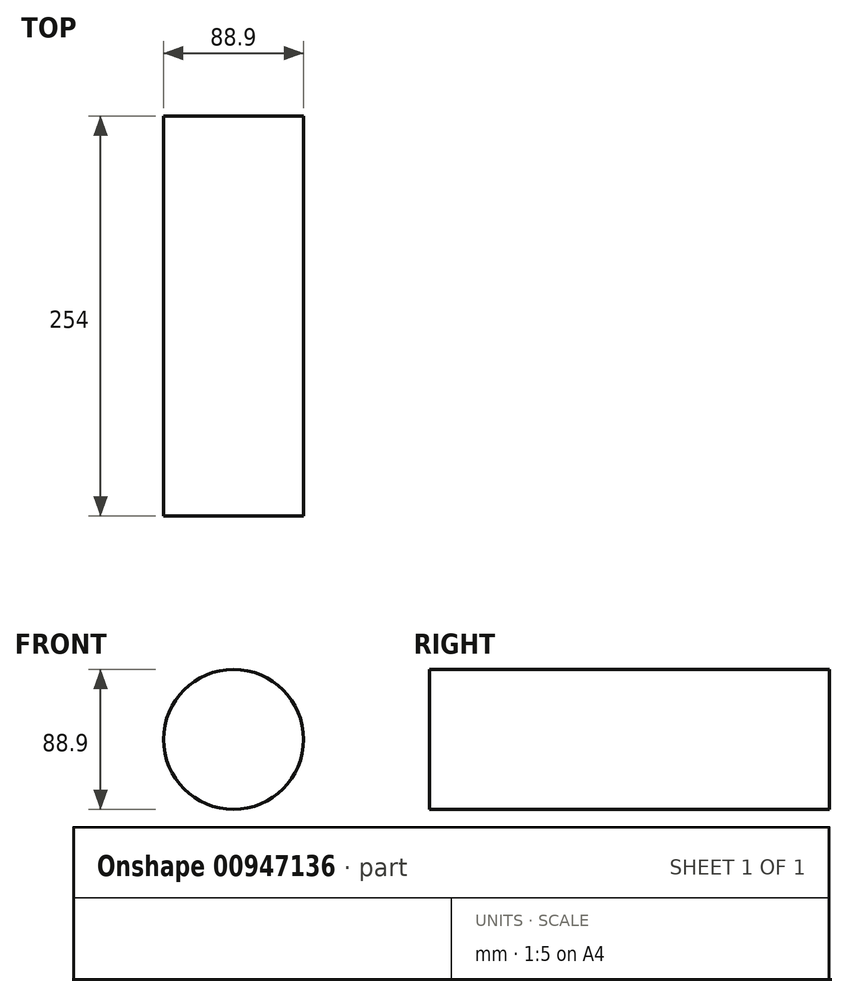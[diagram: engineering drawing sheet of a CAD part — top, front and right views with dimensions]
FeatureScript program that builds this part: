
annotation { "Feature Type Name" : "Feature", "Feature Type Description" : "" }
export const myFeature = defineFeature(function(context is Context, id is Id, definition is map)
    precondition{}
    {
        {
            var Q0;
            Q0=qCreatedBy(makeId("Front.planeOp"),FACE);
            var sketch = newSketch(context, id + "F0", { "sketchPlane" : qUnion([Q0])});
            skCircle(sketch, "E0", {"center": v(0, 0) * mm, "radius": 44.45 * mm});
            skSolve(sketch);
        }
        {
            var Q0;
            Q0=makeQuery(id+"F0.imprint","IMPRINT",FACE,{"disambiguationData":[TD([[makeQuery(id+"F0.imprint","IMPRINT",EDGE,{"derivedFrom":sQuery(id+"F0.wireOp",EDGE,"E0")}),1.0]])]});
            extrude(context, id + "F1", {"entities" : qUnion([Q0]), "depth" : 254 * mm, "offsetDistance" : 25.4 * mm});
        }
    });
